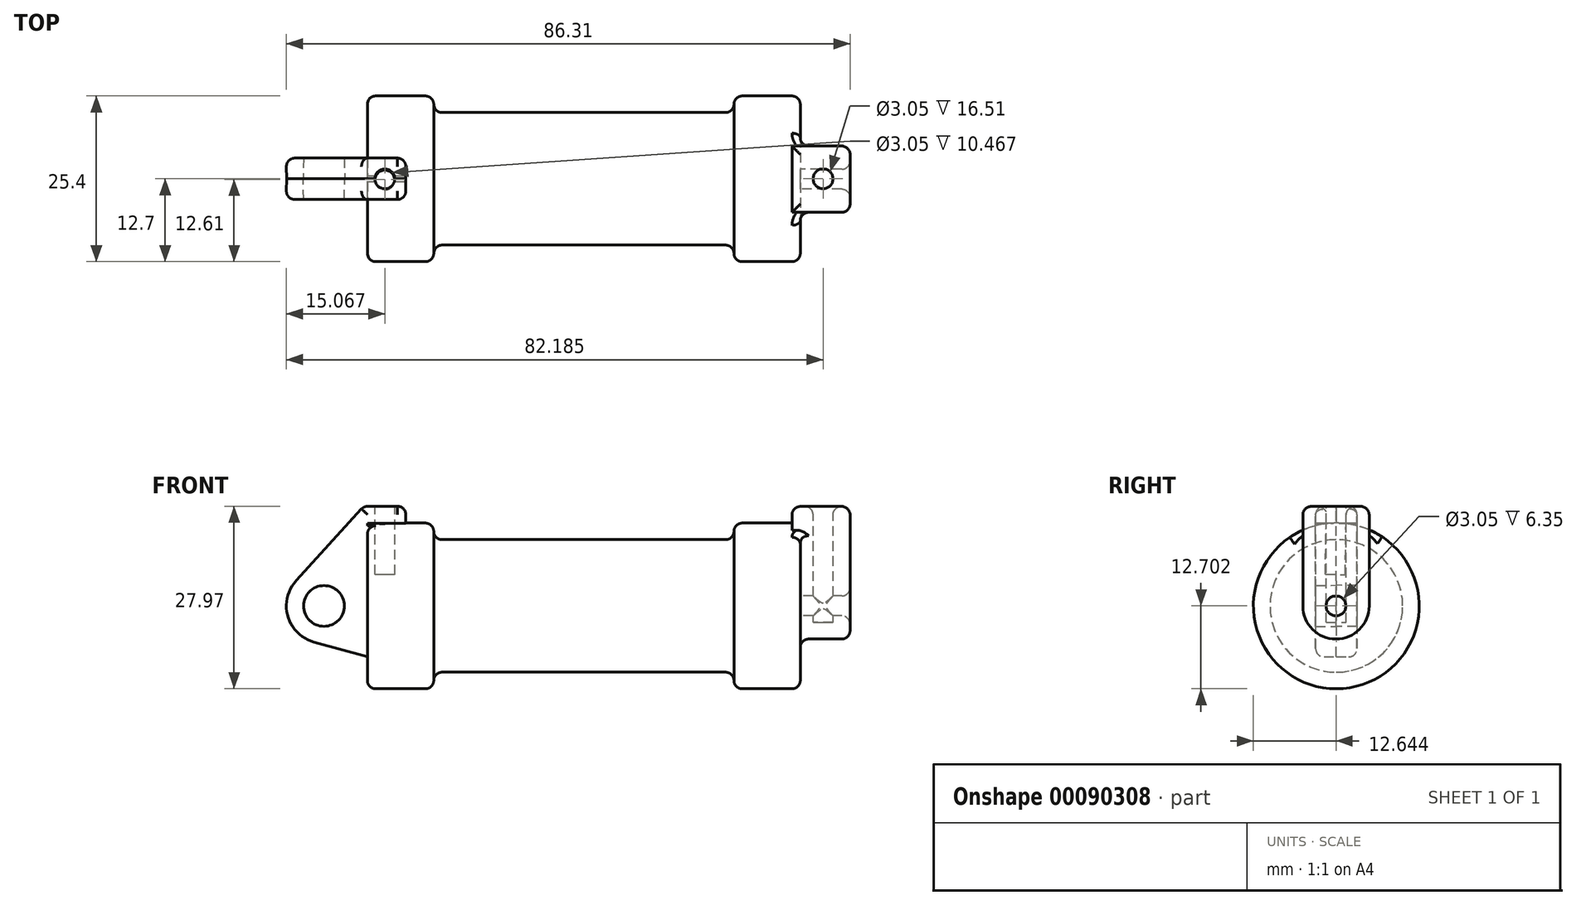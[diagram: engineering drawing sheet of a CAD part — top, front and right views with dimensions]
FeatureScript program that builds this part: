
annotation { "Feature Type Name" : "Feature", "Feature Type Description" : "" }
export const myFeature = defineFeature(function(context is Context, id is Id, definition is map)
    precondition{}
    {
        {
            var Q0;
            Q0=qCreatedBy(makeId("Front.planeOp"),FACE);
            var sketch = newSketch(context, id + "F0", { "sketchPlane" : qUnion([Q0])});
            skLineSegment(sketch, "E0", {"start": v(0, 0) * mm, "end": v(0, 12.7) * mm});
            skLineSegment(sketch, "E1", {"start": v(0, 12.7) * mm, "end": v(10.16, 12.7) * mm});
            skLineSegment(sketch, "E2", {"start": v(10.16, 12.7) * mm, "end": v(10.16, 10.16) * mm});
            skLineSegment(sketch, "E3", {"start": v(10.16, 10.16) * mm, "end": v(56.13, 10.16) * mm});
            skLineSegment(sketch, "E4", {"start": v(56.13, 10.16) * mm, "end": v(56.13, 12.7) * mm});
            skLineSegment(sketch, "E5", {"start": v(56.13, 12.7) * mm, "end": v(66.3, 12.7) * mm});
            skLineSegment(sketch, "E6", {"start": v(66.3, 12.7) * mm, "end": v(66.3, 0) * mm});
            skLineSegment(sketch, "E7", {"start": v(66.3, 0) * mm, "end": v(0, 0) * mm});
            skLineSegment(sketch, "E8", {"start": v(5.84, 15.24) * mm, "end": v(-0.5, 15.24) * mm});
            skLineSegment(sketch, "E9", {"start": v(-0.5, 15.24) * mm, "end": v(-10.88, 3.85) * mm});
            skLineSegment(sketch, "E10", {"start": v(0, 0) * mm, "end": v(-6.65, 0) * mm});
            skCircle(sketch, "E11", {"center": v(-6.65, 0) * mm, "radius": 5.72 * mm});
            skCircle(sketch, "E12", {"center": v(-6.65, 0) * mm, "radius": 3.18 * mm});
            skLineSegment(sketch, "E13", {"start": v(5.84, 15.24) * mm, "end": v(5.84, -9.4) * mm});
            skLineSegment(sketch, "E14", {"start": v(5.84, -9.4) * mm, "end": v(-8.18, -5.5) * mm});
            skSolve(sketch);
        }
        {
            var Q0;
            {var subQ0=sQuery(id+"F0.wireOp",EDGE,"E2");Q0=makeQuery(id+"F0.imprint","IMPRINT",FACE,{"disambiguationData":[TD([[makeQuery(id+"F0.imprint","IMPRINT",EDGE,{"derivedFrom":subQ0}),-1.0]])]});}
            var Q1;
            {var subQ0=sQuery(id+"F0.wireOp",EDGE,"E0");Q1=makeQuery(id+"F0.imprint","IMPRINT",FACE,{"disambiguationData":[TD([[makeQuery(id+"F0.imprint","IMPRINT",EDGE,{"derivedFrom":subQ0}),-1.0]])]});}
            var Q2;
            Q2=sQuery(id+"F0.wireOp",EDGE,"E7");
            revolve(context, id + "F1", {"entities" : qUnion([Q0, Q1]), "axis" : qUnion([Q2]), "revolveType" : RevolveType.FULL});
        }
        {
            var Q0;
            {var subQ3=sQuery(id+"F0.wireOp",EDGE,"E0");Q0=makeQuery(id+"F0.imprint","IMPRINT",FACE,{"disambiguationData":[TD([[makeQuery(id+"F0.imprint","IMPRINT",EDGE,{"derivedFrom":subQ3}),1.0]])]});}
            var Q1;
            {var subQ0=sQuery(id+"F0.wireOp",EDGE,"E14");Q1=makeQuery(id+"F0.imprint","IMPRINT",FACE,{"disambiguationData":[TD([[makeQuery(id+"F0.imprint","IMPRINT",EDGE,{"derivedFrom":subQ0}),-1.0]])]});}
            var Q2;
            {var subQ4=sQuery(id+"F0.wireOp",EDGE,"E12");Q2=makeQuery(id+"F0.imprint","IMPRINT",FACE,{"disambiguationData":[TD([[makeQuery(id+"F0.imprint","IMPRINT",EDGE,{"derivedFrom":subQ4}),-1.0]])]});}
            extrude(context, id + "F2", {"entities" : qUnion([Q0, Q1, Q2]), "operationType" : NewBodyOperationType.ADD, "endBound" : BoundingType.SYMMETRIC, "depth" : 6.35 * mm, "hasDraft" : true, "draftAngle" : 1 * degree});
        }
        {
            var Q0;
            Q0=makeQuery(id+"F1.opRevolve","SWEPT_FACE",FACE,{"disambiguationData":[OSD([sQuery(id+"F0.wireOp",EDGE,"E6")])]});
            var sketch = newSketch(context, id + "F3", { "sketchPlane" : qUnion([Q0])});
            skCircle(sketch, "E15", {"center": v(-0.06, 0) * mm, "radius": 5.08 * mm});
            skCircle(sketch, "E16", {"center": v(-0.06, 0) * mm, "radius": 1.52 * mm});
            skLineSegment(sketch, "E17", {"start": v(-5.14, 0) * mm, "end": v(-5.14, 15.24) * mm});
            skLineSegment(sketch, "E18", {"start": v(5.02, 0) * mm, "end": v(5.02, 15.24) * mm});
            skLineSegment(sketch, "E19", {"start": v(-5.14, 15.24) * mm, "end": v(5.02, 15.24) * mm});
            skSolve(sketch);
        }
        {
            var Q0;
            {var subQ0=sQuery(id+"F3.wireOp",EDGE,"E19");Q0=makeQuery(id+"F3.imprint","IMPRINT",FACE,{"disambiguationData":[TD([[makeQuery(id+"F3.imprint","IMPRINT",EDGE,{"derivedFrom":subQ0}),-1.0]])]});}
            var Q1;
            {var subQ0=sQuery(id+"F3.wireOp",EDGE,"E17");var subQ1=sQuery(id+"F3.wireOp",EDGE,"E15");var subQ2=makeQuery(id+"F3.imprint","INTERSECT",VERTEX,{"derivedFrom":[subQ1,subQ0]});Q1=makeQuery(id+"F3.imprint","IMPRINT",FACE,{"disambiguationData":[TD([[makeQuery(id+"F3.imprint","IMPRINT",EDGE,{"disambiguationData":[TD([[subQ2,1.0]])],"derivedFrom":subQ1}),-1.0]])]});}
            var Q2;
            Q2=makeQuery(id+"F3.imprint","IMPRINT",FACE,{"disambiguationData":[TD([[makeQuery(id+"F3.imprint","IMPRINT",EDGE,{"derivedFrom":sQuery(id+"F3.wireOp",EDGE,"E16")}),-1.0]])]});
            extrude(context, id + "F4", {"entities" : qUnion([Q0, Q1, Q2]), "operationType" : NewBodyOperationType.ADD, "depth" : 7.62 * mm});
        }
        {
            var Q0;
            Q0=makeQuery(id+"F4.opExtrude","CAP_FACE",FACE,{"disambiguationData":[OSD([sQuery(id+"F3.wireOp",EDGE,"E15"),sQuery(id+"F3.wireOp",EDGE,"E16"),sQuery(id+"F3.wireOp",EDGE,"E17"),sQuery(id+"F3.wireOp",EDGE,"E18"),sQuery(id+"F3.wireOp",EDGE,"E19")])],"isStart":true});
            extrude(context, id + "F5", {"entities" : qUnion([Q0]), "operationType" : NewBodyOperationType.ADD, "depth" : 1.27 * mm});
        }
        {
            var Q0;
            {var subQ0=sQuery(id+"F3.wireOp",EDGE,"E19");Q0=makeQuery(id+"F5.boolean.opBoolean","MERGE",FACE,{"derivedFrom":[makeQuery(id+"F4.opExtrude","SWEPT_FACE",FACE,{"disambiguationData":[OSD([subQ0])]}),makeQuery(id+"F5.opExtrude","SWEPT_FACE",FACE,{"disambiguationData":[OSD([subQ0])]})]});}
            var sketch = newSketch(context, id + "F6", { "sketchPlane" : qUnion([Q0])});
            skCircle(sketch, "E20", {"center": v(69.79, 0) * mm, "radius": 1.52 * mm});
            skSolve(sketch);
        }
        {
            var Q0;
            Q0 = qSketchRegion(id + "F6", true);
            extrude(context, id + "F7", {"entities" : qUnion([Q0]), "operationType" : NewBodyOperationType.REMOVE, "oppositeDirection" : true, "depth" : 17.78 * mm});
        }
        {
            var Q0;
            Q0=makeQuery(id+"F2.split0.splitOp","SPLIT",FACE,{"derivedFrom":makeQuery(id+"F2.opExtrude","SWEPT_FACE",FACE,{"disambiguationData":[OSD([sQuery(id+"F0.wireOp",EDGE,"E8")])]})});
            var sketch = newSketch(context, id + "F8", { "sketchPlane" : qUnion([Q0])});
            skCircle(sketch, "E21", {"center": v(2.67, -0.27) * mm, "radius": 1.52 * mm});
            skSolve(sketch);
        }
        {
            var Q0;
            Q0 = qSketchRegion(id + "F8", true);
            extrude(context, id + "F9", {"entities" : qUnion([Q0]), "operationType" : NewBodyOperationType.REMOVE, "oppositeDirection" : true, "depth" : 10.4 * mm});
        }
        {
            var Q0;
            Q0 = qSketchRegion(id + "F8", true);
            extrude(context, id + "F10", {"entities" : qUnion([Q0]), "operationType" : NewBodyOperationType.REMOVE, "depth" : 10.4 * mm});
        }
        {
            var Q0;
            Q0=makeQuery(id+"F1.opRevolve","SWEPT_FACE",FACE,{"disambiguationData":[OSD([sQuery(id+"F0.wireOp",EDGE,"E3")])]});
            fillet(context, id + "F11", {"entities" : qUnion([Q0]), "radius" : 1.27 * mm, "tangentPropagation" : true, "allowEdgeOverflow" : false});
        }
        {
            var Q0;
            Q0=makeQuery(id+"F4.opExtrude","SWEPT_FACE",FACE,{"disambiguationData":[OSD([sQuery(id+"F3.wireOp",EDGE,"E15")])]});
            fillet(context, id + "F12", {"entities" : qUnion([Q0]), "radius" : 1.27 * mm, "tangentPropagation" : true, "allowEdgeOverflow" : false});
        }
        {
            var Q0;
            Q0=makeQuery(id+"F4.boolean.opBoolean","SPLIT",FACE,{"disambiguationData":[TD([makeQuery(id+"F1.opRevolve","SWEPT_FACE",FACE,{"disambiguationData":[OSD([sQuery(id+"F0.wireOp",EDGE,"E5")])]})])],"derivedFrom":makeQuery(id+"F1.opRevolve","SWEPT_FACE",FACE,{"disambiguationData":[OSD([sQuery(id+"F0.wireOp",EDGE,"E6")])]})});
            fillet(context, id + "F13", {"entities" : qUnion([Q0]), "radius" : 1.27 * mm, "tangentPropagation" : true, "allowEdgeOverflow" : false});
        }
        {
            var Q0;
            Q0=makeQuery(id+"F1.opRevolve","SWEPT_EDGE",EDGE,{"disambiguationData":[OSD([sQuery(id+"F0.wireOp",EDGE,"E0"),sQuery(id+"F0.wireOp",EDGE,"E1")])]});
            fillet(context, id + "F14", {"entities" : qUnion([Q0]), "radius" : 1.27 * mm, "tangentPropagation" : true, "allowEdgeOverflow" : false});
        }
        {
            var Q0;
            Q0=makeQuery(id+"F2.opExtrude","CAP_EDGE",EDGE,{"disambiguationData":[OSD([sQuery(id+"F0.wireOp",EDGE,"E9")])],"isStart":true});
            fillet(context, id + "F15", {"entities" : qUnion([Q0]), "radius" : 1.27 * mm, "tangentPropagation" : true, "allowEdgeOverflow" : false});
        }
        {
            var Q0;
            Q0=makeQuery(id+"F2.opExtrude","CAP_EDGE",EDGE,{"disambiguationData":[OSD([sQuery(id+"F0.wireOp",EDGE,"E9")])],"isStart":false});
            fillet(context, id + "F16", {"entities" : qUnion([Q0]), "radius" : 1.27 * mm, "tangentPropagation" : true, "allowEdgeOverflow" : false});
        }
        {
            var Q0;
            Q0=makeQuery(id+"F1.opRevolve","SWEPT_EDGE",EDGE,{"disambiguationData":[OSD([sQuery(id+"F0.wireOp",EDGE,"E1"),sQuery(id+"F0.wireOp",EDGE,"E2")])]});
            fillet(context, id + "F17", {"entities" : qUnion([Q0]), "radius" : 1.27 * mm, "tangentPropagation" : true, "allowEdgeOverflow" : false});
        }
        {
            var Q0;
            {var subQ0=sQuery(id+"F3.wireOp",EDGE,"E19");Q0=makeQuery(id+"F5.boolean.opBoolean","MERGE",FACE,{"derivedFrom":[makeQuery(id+"F4.opExtrude","SWEPT_FACE",FACE,{"disambiguationData":[OSD([subQ0])]}),makeQuery(id+"F5.opExtrude","SWEPT_FACE",FACE,{"disambiguationData":[OSD([subQ0])]})]});}
            var Q1;
            Q1=makeQuery(id+"F4.opExtrude","CAP_FACE",FACE,{"disambiguationData":[OSD([sQuery(id+"F3.wireOp",EDGE,"E15"),sQuery(id+"F3.wireOp",EDGE,"E16"),sQuery(id+"F3.wireOp",EDGE,"E17"),sQuery(id+"F3.wireOp",EDGE,"E18"),sQuery(id+"F3.wireOp",EDGE,"E19")])],"isStart":false});
            fillet(context, id + "F18", {"entities" : qUnion([Q0, Q1]), "radius" : 1.27 * mm, "tangentPropagation" : true, "allowEdgeOverflow" : false});
        }
        {
            var Q0;
            Q0=makeQuery(id+"F2.opExtrude","CAP_EDGE",EDGE,{"disambiguationData":[OSD([sQuery(id+"F0.wireOp",EDGE,"E8")])],"isStart":false});
            var Q1;
            Q1=makeQuery(id+"F2.opExtrude","CAP_EDGE",EDGE,{"disambiguationData":[OSD([sQuery(id+"F0.wireOp",EDGE,"E8")])],"isStart":true});
            var Q2;
            Q2=makeQuery(id+"F15.opFillet","BLEND_EDGE",EDGE,{"blendedFrom":[makeQuery(id+"F2.opExtrude","CAP_EDGE",EDGE,{"disambiguationData":[OSD([sQuery(id+"F0.wireOp",EDGE,"E9")])],"isStart":true}),makeQuery(id+"F2.split0.splitOp","SPLIT",FACE,{"derivedFrom":makeQuery(id+"F2.opExtrude","SWEPT_FACE",FACE,{"disambiguationData":[OSD([sQuery(id+"F0.wireOp",EDGE,"E8")])]}),"isFromBackBody":true})],"blendedInto":[makeQuery(id+"F2.split0.splitOp","SPLIT",FACE,{"derivedFrom":makeQuery(id+"F2.opExtrude","SWEPT_FACE",FACE,{"disambiguationData":[OSD([sQuery(id+"F0.wireOp",EDGE,"E8")])]}),"isFromBackBody":true})]});
            var Q3;
            Q3=makeQuery(id+"F16.opFillet","BLEND_EDGE",EDGE,{"blendedFrom":[makeQuery(id+"F2.opExtrude","CAP_EDGE",EDGE,{"disambiguationData":[OSD([sQuery(id+"F0.wireOp",EDGE,"E9")])],"isStart":false}),makeQuery(id+"F2.split0.splitOp","SPLIT",FACE,{"derivedFrom":makeQuery(id+"F2.opExtrude","SWEPT_FACE",FACE,{"disambiguationData":[OSD([sQuery(id+"F0.wireOp",EDGE,"E8")])]})})],"blendedInto":[makeQuery(id+"F2.split0.splitOp","SPLIT",FACE,{"derivedFrom":makeQuery(id+"F2.opExtrude","SWEPT_FACE",FACE,{"disambiguationData":[OSD([sQuery(id+"F0.wireOp",EDGE,"E8")])]})})]});
            fillet(context, id + "F19", {"entities" : qUnion([Q0, Q1, Q2, Q3]), "radius" : 1.27 * mm, "tangentPropagation" : true, "allowEdgeOverflow" : false});
        }
        {
            var Q0;
            Q0=makeQuery(id+"F2.split0.splitOp","SPLIT",EDGE,{"derivedFrom":makeQuery(id+"F2.opExtrude","SWEPT_EDGE",EDGE,{"disambiguationData":[OSD([sQuery(id+"F0.wireOp",EDGE,"E8"),sQuery(id+"F0.wireOp",EDGE,"E13")])]}),"isFromBackBody":true});
            var Q1;
            {var subQ0=sQuery(id+"F0.wireOp",EDGE,"E13");var subQ1=sQuery(id+"F0.wireOp",EDGE,"E8");Q1=makeQuery(id+"F19.opFillet","BLEND_EDGE",EDGE,{"blendedFrom":[makeQuery(id+"F2.opExtrude","CAP_EDGE",EDGE,{"disambiguationData":[OSD([subQ1])],"isStart":true}),makeQuery(id+"F2.split0.splitOp","SPLIT",FACE,{"derivedFrom":makeQuery(id+"F2.opExtrude","SWEPT_FACE",FACE,{"disambiguationData":[OSD([subQ0]),TDD([makeQuery(id+"F0.imprint","IMPRINT",EDGE,{"disambiguationData":[TD([[makeQuery(id+"F0.imprint","INTERSECT",VERTEX,{"derivedFrom":[subQ1,subQ0]}),-1.0]])],"derivedFrom":subQ0})])]}),"isFromBackBody":true})],"blendedInto":[makeQuery(id+"F2.split0.splitOp","SPLIT",FACE,{"derivedFrom":makeQuery(id+"F2.opExtrude","SWEPT_FACE",FACE,{"disambiguationData":[OSD([subQ0]),TDD([makeQuery(id+"F0.imprint","IMPRINT",EDGE,{"disambiguationData":[TD([[makeQuery(id+"F0.imprint","INTERSECT",VERTEX,{"derivedFrom":[subQ1,subQ0]}),-1.0]])],"derivedFrom":subQ0})])]}),"isFromBackBody":true})]});}
            var Q2;
            Q2=makeQuery(id+"F2.split0.splitOp","SPLIT",EDGE,{"derivedFrom":makeQuery(id+"F2.opExtrude","SWEPT_EDGE",EDGE,{"disambiguationData":[OSD([sQuery(id+"F0.wireOp",EDGE,"E8"),sQuery(id+"F0.wireOp",EDGE,"E13")])]})});
            var Q3;
            {var subQ0=sQuery(id+"F0.wireOp",EDGE,"E13");var subQ1=sQuery(id+"F0.wireOp",EDGE,"E8");Q3=makeQuery(id+"F19.opFillet","BLEND_EDGE",EDGE,{"blendedFrom":[makeQuery(id+"F2.opExtrude","CAP_EDGE",EDGE,{"disambiguationData":[OSD([subQ1])],"isStart":false}),makeQuery(id+"F2.split0.splitOp","SPLIT",FACE,{"derivedFrom":makeQuery(id+"F2.opExtrude","SWEPT_FACE",FACE,{"disambiguationData":[OSD([subQ0]),TDD([makeQuery(id+"F0.imprint","IMPRINT",EDGE,{"disambiguationData":[TD([[makeQuery(id+"F0.imprint","INTERSECT",VERTEX,{"derivedFrom":[subQ1,subQ0]}),-1.0]])],"derivedFrom":subQ0})])]})})],"blendedInto":[makeQuery(id+"F2.split0.splitOp","SPLIT",FACE,{"derivedFrom":makeQuery(id+"F2.opExtrude","SWEPT_FACE",FACE,{"disambiguationData":[OSD([subQ0]),TDD([makeQuery(id+"F0.imprint","IMPRINT",EDGE,{"disambiguationData":[TD([[makeQuery(id+"F0.imprint","INTERSECT",VERTEX,{"derivedFrom":[subQ1,subQ0]}),-1.0]])],"derivedFrom":subQ0})])]})})]});}
            var Q4;
            {var subQ0=sQuery(id+"F0.wireOp",EDGE,"E8");Q4=makeQuery(id+"F19.opFillet","BLEND_EDGE",EDGE,{"blendedFrom":[makeQuery(id+"F2.opExtrude","CAP_EDGE",EDGE,{"disambiguationData":[OSD([subQ0])],"isStart":true}),makeQuery(id+"F2.opExtrude","CAP_FACE",FACE,{"disambiguationData":[OSD([sQuery(id+"F0.wireOp",EDGE,"E0"),sQuery(id+"F0.wireOp",EDGE,"E1"),sQuery(id+"F0.wireOp",EDGE,"E7"),subQ0,sQuery(id+"F0.wireOp",EDGE,"E9"),sQuery(id+"F0.wireOp",EDGE,"E11"),sQuery(id+"F0.wireOp",EDGE,"E12"),sQuery(id+"F0.wireOp",EDGE,"E13"),sQuery(id+"F0.wireOp",EDGE,"E14")])],"isStart":true})],"blendedInto":[makeQuery(id+"F2.opExtrude","CAP_FACE",FACE,{"disambiguationData":[OSD([sQuery(id+"F0.wireOp",EDGE,"E0"),sQuery(id+"F0.wireOp",EDGE,"E1"),sQuery(id+"F0.wireOp",EDGE,"E7"),subQ0,sQuery(id+"F0.wireOp",EDGE,"E9"),sQuery(id+"F0.wireOp",EDGE,"E11"),sQuery(id+"F0.wireOp",EDGE,"E12"),sQuery(id+"F0.wireOp",EDGE,"E13"),sQuery(id+"F0.wireOp",EDGE,"E14")])],"isStart":true})]});}
            var Q5;
            {var subQ0=sQuery(id+"F0.wireOp",EDGE,"E8");Q5=makeQuery(id+"F19.opFillet","BLEND_EDGE",EDGE,{"blendedFrom":[makeQuery(id+"F2.opExtrude","CAP_EDGE",EDGE,{"disambiguationData":[OSD([subQ0])],"isStart":false}),makeQuery(id+"F2.opExtrude","CAP_FACE",FACE,{"disambiguationData":[OSD([sQuery(id+"F0.wireOp",EDGE,"E0"),sQuery(id+"F0.wireOp",EDGE,"E1"),sQuery(id+"F0.wireOp",EDGE,"E7"),subQ0,sQuery(id+"F0.wireOp",EDGE,"E9"),sQuery(id+"F0.wireOp",EDGE,"E11"),sQuery(id+"F0.wireOp",EDGE,"E12"),sQuery(id+"F0.wireOp",EDGE,"E13"),sQuery(id+"F0.wireOp",EDGE,"E14")])],"isStart":false})],"blendedInto":[makeQuery(id+"F2.opExtrude","CAP_FACE",FACE,{"disambiguationData":[OSD([sQuery(id+"F0.wireOp",EDGE,"E0"),sQuery(id+"F0.wireOp",EDGE,"E1"),sQuery(id+"F0.wireOp",EDGE,"E7"),subQ0,sQuery(id+"F0.wireOp",EDGE,"E9"),sQuery(id+"F0.wireOp",EDGE,"E11"),sQuery(id+"F0.wireOp",EDGE,"E12"),sQuery(id+"F0.wireOp",EDGE,"E13"),sQuery(id+"F0.wireOp",EDGE,"E14")])],"isStart":false})]});}
            var Q6;
            {var subQ0=sQuery(id+"F0.wireOp",EDGE,"E9");Q6=makeQuery(id+"F19.opFillet","BLEND_EDGE",EDGE,{"blendedFrom":[makeQuery(id+"F16.opFillet","BLEND_EDGE",EDGE,{"blendedFrom":[makeQuery(id+"F2.opExtrude","CAP_EDGE",EDGE,{"disambiguationData":[OSD([subQ0])],"isStart":false}),makeQuery(id+"F2.split0.splitOp","SPLIT",FACE,{"derivedFrom":makeQuery(id+"F2.opExtrude","SWEPT_FACE",FACE,{"disambiguationData":[OSD([sQuery(id+"F0.wireOp",EDGE,"E8")])]})})],"blendedInto":[makeQuery(id+"F2.split0.splitOp","SPLIT",FACE,{"derivedFrom":makeQuery(id+"F2.opExtrude","SWEPT_FACE",FACE,{"disambiguationData":[OSD([sQuery(id+"F0.wireOp",EDGE,"E8")])]})})]}),makeQuery(id+"F16.opFillet","BLEND_FACE",FACE,{"disambiguationData":[OSD([subQ0])]})],"blendedInto":[makeQuery(id+"F16.opFillet","BLEND_FACE",FACE,{"disambiguationData":[OSD([subQ0])]})]});}
            var Q7;
            {var subQ0=sQuery(id+"F0.wireOp",EDGE,"E9");Q7=makeQuery(id+"F19.opFillet","BLEND_EDGE",EDGE,{"blendedFrom":[makeQuery(id+"F2.split0.splitOp","SPLIT",EDGE,{"derivedFrom":makeQuery(id+"F2.opExtrude","SWEPT_EDGE",EDGE,{"disambiguationData":[OSD([sQuery(id+"F0.wireOp",EDGE,"E8"),subQ0])]})}),makeQuery(id+"F2.split0.splitOp","SPLIT",FACE,{"derivedFrom":makeQuery(id+"F2.opExtrude","SWEPT_FACE",FACE,{"disambiguationData":[OSD([subQ0])]})})],"blendedInto":[makeQuery(id+"F2.split0.splitOp","SPLIT",FACE,{"derivedFrom":makeQuery(id+"F2.opExtrude","SWEPT_FACE",FACE,{"disambiguationData":[OSD([subQ0])]})})]});}
            var Q8;
            {var subQ0=sQuery(id+"F0.wireOp",EDGE,"E9");Q8=makeQuery(id+"F19.opFillet","BLEND_EDGE",EDGE,{"blendedFrom":[makeQuery(id+"F2.split0.splitOp","SPLIT",EDGE,{"derivedFrom":makeQuery(id+"F2.opExtrude","SWEPT_EDGE",EDGE,{"disambiguationData":[OSD([sQuery(id+"F0.wireOp",EDGE,"E8"),subQ0])]}),"isFromBackBody":true}),makeQuery(id+"F2.split0.splitOp","SPLIT",FACE,{"derivedFrom":makeQuery(id+"F2.opExtrude","SWEPT_FACE",FACE,{"disambiguationData":[OSD([subQ0])]}),"isFromBackBody":true})],"blendedInto":[makeQuery(id+"F2.split0.splitOp","SPLIT",FACE,{"derivedFrom":makeQuery(id+"F2.opExtrude","SWEPT_FACE",FACE,{"disambiguationData":[OSD([subQ0])]}),"isFromBackBody":true})]});}
            var Q9;
            {var subQ0=sQuery(id+"F0.wireOp",EDGE,"E9");Q9=makeQuery(id+"F19.opFillet","BLEND_EDGE",EDGE,{"blendedFrom":[makeQuery(id+"F15.opFillet","BLEND_EDGE",EDGE,{"blendedFrom":[makeQuery(id+"F2.opExtrude","CAP_EDGE",EDGE,{"disambiguationData":[OSD([subQ0])],"isStart":true}),makeQuery(id+"F2.split0.splitOp","SPLIT",FACE,{"derivedFrom":makeQuery(id+"F2.opExtrude","SWEPT_FACE",FACE,{"disambiguationData":[OSD([sQuery(id+"F0.wireOp",EDGE,"E8")])]}),"isFromBackBody":true})],"blendedInto":[makeQuery(id+"F2.split0.splitOp","SPLIT",FACE,{"derivedFrom":makeQuery(id+"F2.opExtrude","SWEPT_FACE",FACE,{"disambiguationData":[OSD([sQuery(id+"F0.wireOp",EDGE,"E8")])]}),"isFromBackBody":true})]}),makeQuery(id+"F15.opFillet","BLEND_FACE",FACE,{"disambiguationData":[OSD([subQ0])]})],"blendedInto":[makeQuery(id+"F15.opFillet","BLEND_FACE",FACE,{"disambiguationData":[OSD([subQ0])]})]});}
            fillet(context, id + "F20", {"entities" : qUnion([Q0, Q1, Q2, Q3, Q4, Q5, Q6, Q7, Q8, Q9]), "radius" : 1.27 * mm, "tangentPropagation" : true, "allowEdgeOverflow" : false});
        }
        {
            var Q0;
            Q0=makeQuery(id+"F1.opRevolve","SWEPT_EDGE",EDGE,{"disambiguationData":[OSD([sQuery(id+"F0.wireOp",EDGE,"E4"),sQuery(id+"F0.wireOp",EDGE,"E5")])]});
            fillet(context, id + "F21", {"entities" : qUnion([Q0]), "radius" : 1.27 * mm, "tangentPropagation" : true, "allowEdgeOverflow" : false});
        }
    });
